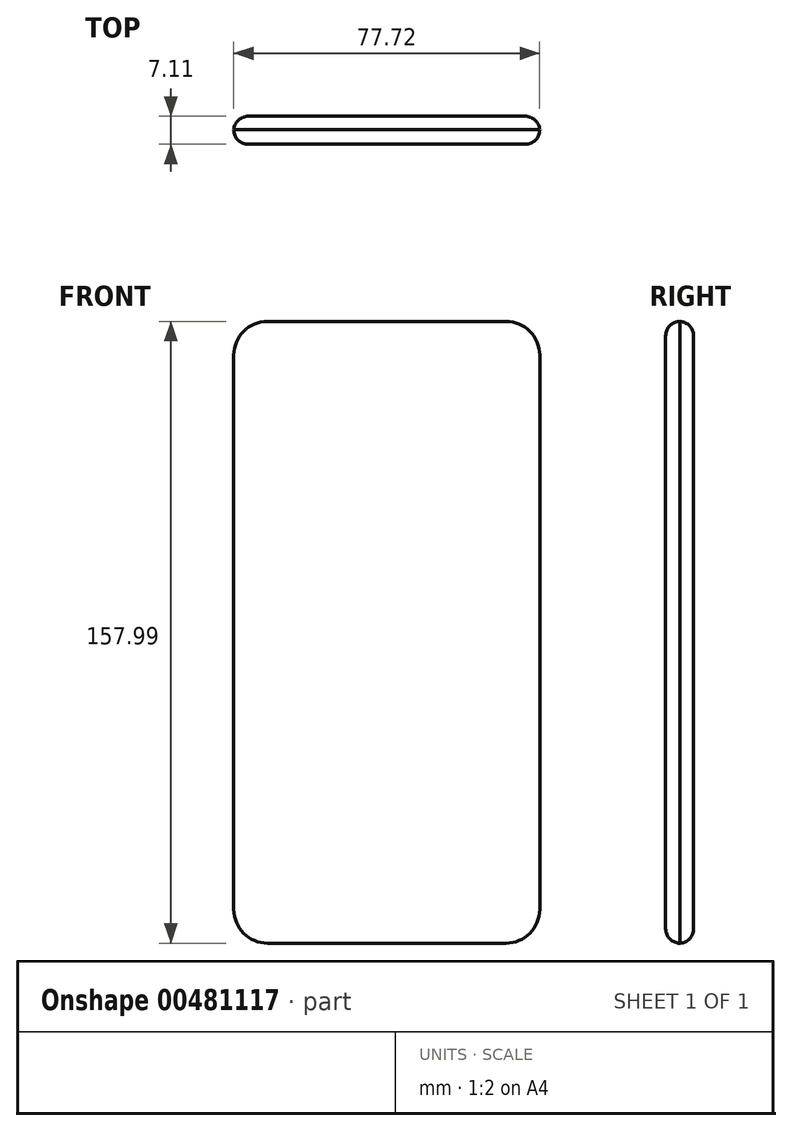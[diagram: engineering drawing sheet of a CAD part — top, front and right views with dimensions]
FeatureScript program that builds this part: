
annotation { "Feature Type Name" : "Feature", "Feature Type Description" : "" }
export const myFeature = defineFeature(function(context is Context, id is Id, definition is map)
    precondition{}
    {
        {
            var Q0;
            Q0=qCreatedBy(makeId("Front.planeOp"),FACE);
            var sketch = newSketch(context, id + "F0", { "sketchPlane" : qUnion([Q0])});
            skLineSegment(sketch, "E0.bottom", {"start": v(-48.55, 50.44) * mm, "end": v(29.17, 50.44) * mm});
            skLineSegment(sketch, "E0.top", {"start": v(-48.55, -107.55) * mm, "end": v(29.17, -107.55) * mm});
            skLineSegment(sketch, "E0.left", {"start": v(-48.55, 50.44) * mm, "end": v(-48.55, -107.55) * mm});
            skLineSegment(sketch, "E0.right", {"start": v(29.17, 50.44) * mm, "end": v(29.17, -107.55) * mm});
            skSolve(sketch);
        }
        {
            var Q0;
            Q0=makeQuery(id+"F0.imprint","IMPRINT",FACE,{"disambiguationData":[TD([[makeQuery(id+"F0.imprint","IMPRINT",EDGE,{"derivedFrom":sQuery(id+"F0.wireOp",EDGE,"E0.bottom")}),-1.0]])]});
            extrude(context, id + "F1", {"entities" : qUnion([Q0]), "depth" : 7.11 * mm});
        }
        {
            var Q0;
            Q0=makeQuery(id+"F1.opExtrude","SWEPT_EDGE",EDGE,{"disambiguationData":[OSD([sQuery(id+"F0.wireOp",EDGE,"E0.bottom"),sQuery(id+"F0.wireOp",EDGE,"E0.left")])]});
            var Q1;
            Q1=makeQuery(id+"F1.opExtrude","SWEPT_EDGE",EDGE,{"disambiguationData":[OSD([sQuery(id+"F0.wireOp",EDGE,"E0.top"),sQuery(id+"F0.wireOp",EDGE,"E0.left")])]});
            var Q2;
            Q2=makeQuery(id+"F1.opExtrude","SWEPT_EDGE",EDGE,{"disambiguationData":[OSD([sQuery(id+"F0.wireOp",EDGE,"E0.top"),sQuery(id+"F0.wireOp",EDGE,"E0.right")])]});
            var Q3;
            Q3=makeQuery(id+"F1.opExtrude","SWEPT_EDGE",EDGE,{"disambiguationData":[OSD([sQuery(id+"F0.wireOp",EDGE,"E0.bottom"),sQuery(id+"F0.wireOp",EDGE,"E0.right")])]});
            fillet(context, id + "F2", {"entities" : qUnion([Q0, Q1, Q2, Q3]), "radius" : 8.58 * mm, "tangentPropagation" : true, "allowEdgeOverflow" : false});
        }
        {
            var Q0;
            Q0=makeQuery(id+"F1.opExtrude","CAP_EDGE",EDGE,{"disambiguationData":[OSD([sQuery(id+"F0.wireOp",EDGE,"E0.bottom")])],"isStart":false});
            fillet(context, id + "F3", {"entities" : qUnion([Q0]), "radius" : 3.68 * mm, "tangentPropagation" : true, "allowEdgeOverflow" : false});
        }
        {
            var Q0;
            Q0=makeQuery(id+"F1.opExtrude","CAP_EDGE",EDGE,{"disambiguationData":[OSD([sQuery(id+"F0.wireOp",EDGE,"E0.bottom")])],"isStart":true});
            fillet(context, id + "F4", {"entities" : qUnion([Q0]), "radius" : 3.68 * mm, "tangentPropagation" : true, "allowEdgeOverflow" : false});
        }
    });
